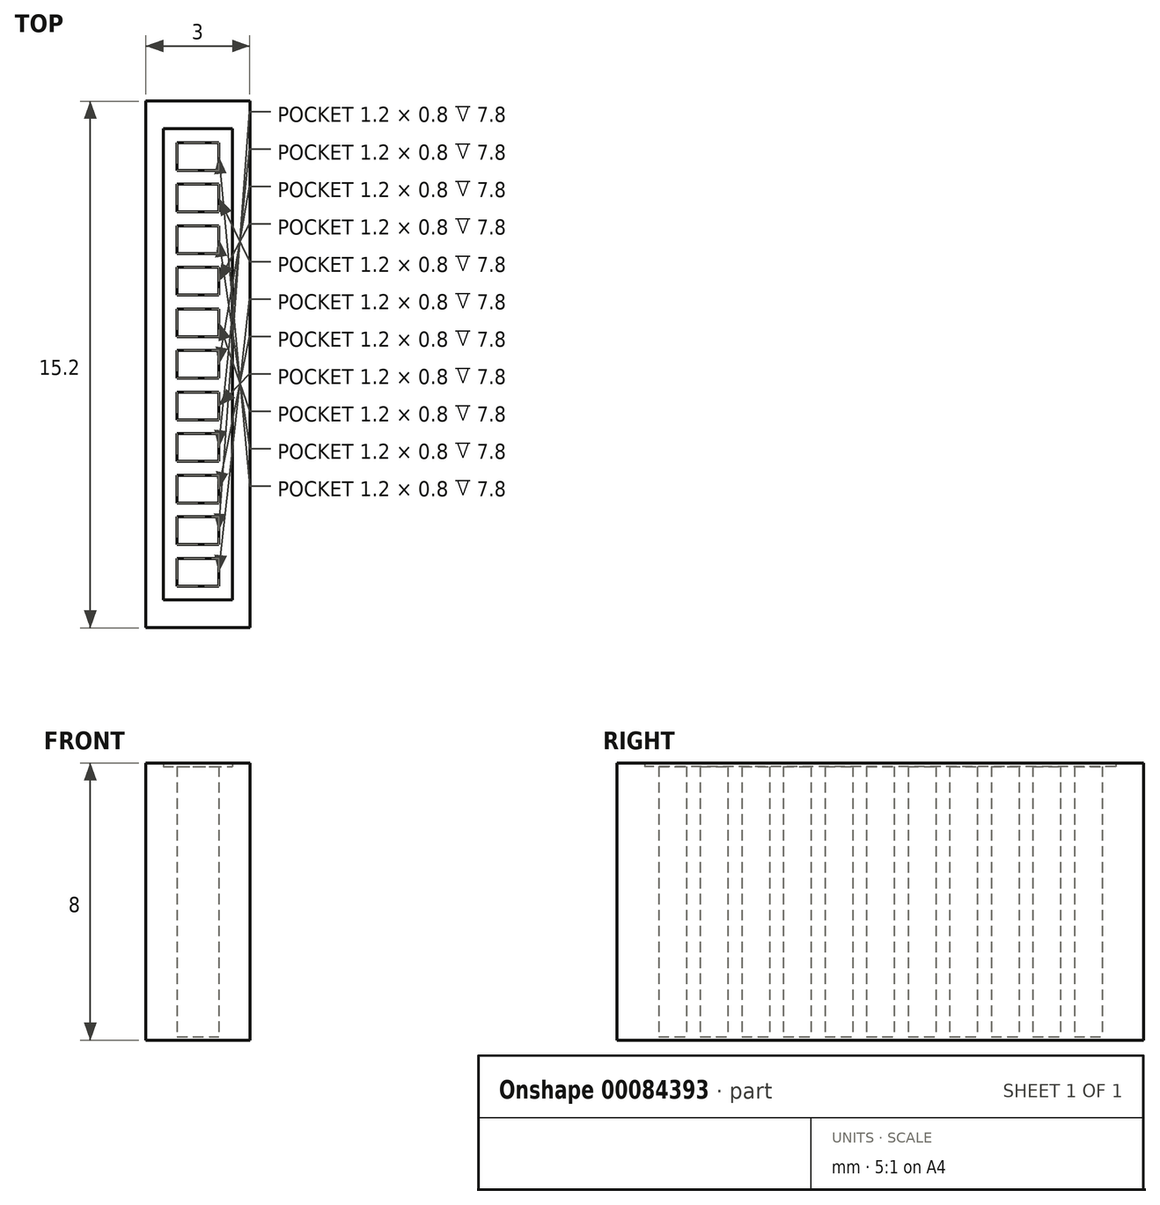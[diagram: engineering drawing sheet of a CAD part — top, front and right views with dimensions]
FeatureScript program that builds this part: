
annotation { "Feature Type Name" : "Feature", "Feature Type Description" : "" }
export const myFeature = defineFeature(function(context is Context, id is Id, definition is map)
    precondition{}
    {
        {
            var Q0;
            Q0=qCreatedBy(makeId("Top.planeOp"),FACE);
            var sketch = newSketch(context, id + "F0", { "sketchPlane" : qUnion([Q0])});
            skLineSegment(sketch, "E0.top", {"start": v(-120.69, 3.96) * mm, "end": v(-117.69, 3.96) * mm});
            skLineSegment(sketch, "E1", {"start": v(-120.19, 4.76) * mm, "end": v(-118.19, 4.76) * mm});
            skLineSegment(sketch, "E2", {"start": v(-120.19, 6.36) * mm, "end": v(-118.19, 6.36) * mm});
            skLineSegment(sketch, "E3", {"start": v(-120.19, 7.16) * mm, "end": v(-118.19, 7.16) * mm});
            skLineSegment(sketch, "E4", {"start": v(-120.19, 8.76) * mm, "end": v(-118.19, 8.76) * mm});
            skLineSegment(sketch, "E5", {"start": v(-120.19, 9.56) * mm, "end": v(-118.19, 9.56) * mm});
            skLineSegment(sketch, "E6", {"start": v(-120.19, 11.16) * mm, "end": v(-118.19, 11.16) * mm});
            skLineSegment(sketch, "E7", {"start": v(-120.19, 11.96) * mm, "end": v(-118.19, 11.96) * mm});
            skLineSegment(sketch, "E8", {"start": v(-120.19, 13.56) * mm, "end": v(-118.19, 13.56) * mm});
            skLineSegment(sketch, "E9", {"start": v(-120.19, 14.36) * mm, "end": v(-118.19, 14.36) * mm});
            skLineSegment(sketch, "E10", {"start": v(-120.19, 15.96) * mm, "end": v(-118.19, 15.96) * mm});
            skLineSegment(sketch, "E11", {"start": v(-120.19, 16.76) * mm, "end": v(-118.19, 16.76) * mm});
            skLineSegment(sketch, "E12", {"start": v(-120.19, 18.36) * mm, "end": v(-118.19, 18.36) * mm});
            skLineSegment(sketch, "E13", {"start": v(-120.19, 19.16) * mm, "end": v(-118.19, 19.16) * mm});
            skLineSegment(sketch, "E14", {"start": v(-120.19, 5.16) * mm, "end": v(-118.19, 5.16) * mm});
            skLineSegment(sketch, "E15", {"start": v(-120.19, 5.96) * mm, "end": v(-118.19, 5.96) * mm});
            skLineSegment(sketch, "E16", {"start": v(-120.19, 7.56) * mm, "end": v(-118.19, 7.56) * mm});
            skLineSegment(sketch, "E17", {"start": v(-120.19, 8.36) * mm, "end": v(-118.19, 8.36) * mm});
            skLineSegment(sketch, "E18", {"start": v(-120.19, 9.96) * mm, "end": v(-118.19, 9.96) * mm});
            skLineSegment(sketch, "E19", {"start": v(-120.19, 10.76) * mm, "end": v(-118.19, 10.76) * mm});
            skLineSegment(sketch, "E20", {"start": v(-120.19, 12.36) * mm, "end": v(-118.19, 12.36) * mm});
            skLineSegment(sketch, "E21", {"start": v(-120.19, 13.16) * mm, "end": v(-118.19, 13.16) * mm});
            skLineSegment(sketch, "E22", {"start": v(-120.19, 14.76) * mm, "end": v(-118.19, 14.76) * mm});
            skLineSegment(sketch, "E23", {"start": v(-120.19, 17.16) * mm, "end": v(-118.19, 17.16) * mm});
            skLineSegment(sketch, "E24", {"start": v(-120.19, 17.96) * mm, "end": v(-118.19, 17.96) * mm});
            skLineSegment(sketch, "E25", {"start": v(-120.19, 15.56) * mm, "end": v(-118.19, 15.56) * mm});
            skLineSegment(sketch, "E26", {"start": v(-117.69, 3.96) * mm, "end": v(-117.69, 19.16) * mm});
            skLineSegment(sketch, "E27", {"start": v(-118.19, 3.96) * mm, "end": v(-118.19, 19.16) * mm});
            skLineSegment(sketch, "E28", {"start": v(-120.69, 3.96) * mm, "end": v(-120.69, 19.16) * mm});
            skLineSegment(sketch, "E29", {"start": v(-120.19, 19.16) * mm, "end": v(-120.19, 3.96) * mm});
            skLineSegment(sketch, "E30", {"start": v(-119.79, 3.96) * mm, "end": v(-119.79, 19.16) * mm});
            skLineSegment(sketch, "E31", {"start": v(-118.59, 3.96) * mm, "end": v(-118.59, 19.16) * mm});
            skLineSegment(sketch, "E32", {"start": v(-120.69, 19.16) * mm, "end": v(-117.69, 19.16) * mm});
            skSolve(sketch);
        }
        {
            var Q0;
            {var subQ0=sQuery(id+"F0.wireOp",EDGE,"E29");var subQ1=sQuery(id+"F0.wireOp",EDGE,"E0.top");var subQ2=makeQuery(id+"F0.imprint","INTERSECT",VERTEX,{"derivedFrom":[subQ1,subQ0]});Q0=makeQuery(id+"F0.imprint","IMPRINT",FACE,{"disambiguationData":[TD([[makeQuery(id+"F0.imprint","IMPRINT",EDGE,{"disambiguationData":[TD([[subQ2,-1.0]])],"derivedFrom":subQ1}),1.0]])]});}
            var Q1;
            {var subQ20=sQuery(id+"F0.wireOp",EDGE,"E28");Q1=makeQuery(id+"F0.imprint","IMPRINT",FACE,{"disambiguationData":[TD([[makeQuery(id+"F0.imprint","IMPRINT",EDGE,{"derivedFrom":subQ20}),-1.0]])]});}
            var Q2;
            {var subQ0=sQuery(id+"F0.wireOp",EDGE,"E30");var subQ1=sQuery(id+"F0.wireOp",EDGE,"E0.top");var subQ2=makeQuery(id+"F0.imprint","INTERSECT",VERTEX,{"derivedFrom":[subQ1,subQ0]});Q2=makeQuery(id+"F0.imprint","IMPRINT",FACE,{"disambiguationData":[TD([[makeQuery(id+"F0.imprint","IMPRINT",EDGE,{"disambiguationData":[TD([[subQ2,-1.0]])],"derivedFrom":subQ1}),1.0]])]});}
            var Q3;
            {var subQ0=sQuery(id+"F0.wireOp",EDGE,"E27");var subQ1=sQuery(id+"F0.wireOp",EDGE,"E0.top");var subQ2=makeQuery(id+"F0.imprint","INTERSECT",VERTEX,{"derivedFrom":[subQ1,subQ0]});Q3=makeQuery(id+"F0.imprint","IMPRINT",FACE,{"disambiguationData":[TD([[makeQuery(id+"F0.imprint","IMPRINT",EDGE,{"disambiguationData":[TD([[subQ2,1.0]])],"derivedFrom":subQ1}),1.0]])]});}
            var Q4;
            {var subQ0=sQuery(id+"F0.wireOp",EDGE,"E29");var subQ1=sQuery(id+"F0.wireOp",EDGE,"E12");var subQ2=makeQuery(id+"F0.imprint","INTERSECT",VERTEX,{"derivedFrom":[subQ1,subQ0]});Q4=makeQuery(id+"F0.imprint","IMPRINT",FACE,{"disambiguationData":[TD([[makeQuery(id+"F0.imprint","IMPRINT",EDGE,{"disambiguationData":[TD([[subQ2,-1.0]])],"derivedFrom":subQ1}),1.0]])]});}
            var Q5;
            {var subQ0=sQuery(id+"F0.wireOp",EDGE,"E30");var subQ1=sQuery(id+"F0.wireOp",EDGE,"E12");var subQ2=makeQuery(id+"F0.imprint","INTERSECT",VERTEX,{"derivedFrom":[subQ1,subQ0]});Q5=makeQuery(id+"F0.imprint","IMPRINT",FACE,{"disambiguationData":[TD([[makeQuery(id+"F0.imprint","IMPRINT",EDGE,{"disambiguationData":[TD([[subQ2,-1.0]])],"derivedFrom":subQ1}),1.0]])]});}
            var Q6;
            {var subQ0=sQuery(id+"F0.wireOp",EDGE,"E27");var subQ1=sQuery(id+"F0.wireOp",EDGE,"E12");var subQ2=makeQuery(id+"F0.imprint","INTERSECT",VERTEX,{"derivedFrom":[subQ1,subQ0]});Q6=makeQuery(id+"F0.imprint","IMPRINT",FACE,{"disambiguationData":[TD([[makeQuery(id+"F0.imprint","IMPRINT",EDGE,{"disambiguationData":[TD([[subQ2,1.0]])],"derivedFrom":subQ1}),1.0]])]});}
            var Q7;
            {var subQ26=sQuery(id+"F0.wireOp",EDGE,"E26");Q7=makeQuery(id+"F0.imprint","IMPRINT",FACE,{"disambiguationData":[TD([[makeQuery(id+"F0.imprint","IMPRINT",EDGE,{"derivedFrom":subQ26}),1.0]])]});}
            extrude(context, id + "F1", {"entities" : qUnion([Q0, Q1, Q2, Q3, Q4, Q5, Q6, Q7]), "depth" : 8 * mm});
        }
        {
            var Q0;
            {var subQ0=sQuery(id+"F0.wireOp",EDGE,"E29");var subQ1=sQuery(id+"F0.wireOp",EDGE,"E1");var subQ2=makeQuery(id+"F0.imprint","INTERSECT",VERTEX,{"derivedFrom":[subQ1,subQ0]});Q0=makeQuery(id+"F0.imprint","IMPRINT",FACE,{"disambiguationData":[TD([[makeQuery(id+"F0.imprint","IMPRINT",EDGE,{"disambiguationData":[TD([[subQ2,-1.0]])],"derivedFrom":subQ1}),1.0]])]});}
            var Q1;
            {var subQ0=sQuery(id+"F0.wireOp",EDGE,"E30");var subQ1=sQuery(id+"F0.wireOp",EDGE,"E1");var subQ2=makeQuery(id+"F0.imprint","INTERSECT",VERTEX,{"derivedFrom":[subQ1,subQ0]});Q1=makeQuery(id+"F0.imprint","IMPRINT",FACE,{"disambiguationData":[TD([[makeQuery(id+"F0.imprint","IMPRINT",EDGE,{"disambiguationData":[TD([[subQ2,-1.0]])],"derivedFrom":subQ1}),1.0]])]});}
            var Q2;
            {var subQ0=sQuery(id+"F0.wireOp",EDGE,"E27");var subQ1=sQuery(id+"F0.wireOp",EDGE,"E1");var subQ2=makeQuery(id+"F0.imprint","INTERSECT",VERTEX,{"derivedFrom":[subQ1,subQ0]});Q2=makeQuery(id+"F0.imprint","IMPRINT",FACE,{"disambiguationData":[TD([[makeQuery(id+"F0.imprint","IMPRINT",EDGE,{"disambiguationData":[TD([[subQ2,1.0]])],"derivedFrom":subQ1}),1.0]])]});}
            var Q3;
            {var subQ0=sQuery(id+"F0.wireOp",EDGE,"E27");var subQ1=sQuery(id+"F0.wireOp",EDGE,"E14");var subQ2=makeQuery(id+"F0.imprint","INTERSECT",VERTEX,{"derivedFrom":[subQ1,subQ0]});Q3=makeQuery(id+"F0.imprint","IMPRINT",FACE,{"disambiguationData":[TD([[makeQuery(id+"F0.imprint","IMPRINT",EDGE,{"disambiguationData":[TD([[subQ2,1.0]])],"derivedFrom":subQ1}),1.0]])]});}
            var Q4;
            {var subQ0=sQuery(id+"F0.wireOp",EDGE,"E27");var subQ1=sQuery(id+"F0.wireOp",EDGE,"E2");var subQ2=makeQuery(id+"F0.imprint","INTERSECT",VERTEX,{"derivedFrom":[subQ1,subQ0]});Q4=makeQuery(id+"F0.imprint","IMPRINT",FACE,{"disambiguationData":[TD([[makeQuery(id+"F0.imprint","IMPRINT",EDGE,{"disambiguationData":[TD([[subQ2,1.0]])],"derivedFrom":subQ1}),-1.0]])]});}
            var Q5;
            {var subQ0=sQuery(id+"F0.wireOp",EDGE,"E30");var subQ1=sQuery(id+"F0.wireOp",EDGE,"E2");var subQ2=makeQuery(id+"F0.imprint","INTERSECT",VERTEX,{"derivedFrom":[subQ1,subQ0]});Q5=makeQuery(id+"F0.imprint","IMPRINT",FACE,{"disambiguationData":[TD([[makeQuery(id+"F0.imprint","IMPRINT",EDGE,{"disambiguationData":[TD([[subQ2,-1.0]])],"derivedFrom":subQ1}),-1.0]])]});}
            var Q6;
            {var subQ0=sQuery(id+"F0.wireOp",EDGE,"E29");var subQ1=sQuery(id+"F0.wireOp",EDGE,"E2");var subQ2=makeQuery(id+"F0.imprint","INTERSECT",VERTEX,{"derivedFrom":[subQ1,subQ0]});Q6=makeQuery(id+"F0.imprint","IMPRINT",FACE,{"disambiguationData":[TD([[makeQuery(id+"F0.imprint","IMPRINT",EDGE,{"disambiguationData":[TD([[subQ2,-1.0]])],"derivedFrom":subQ1}),-1.0]])]});}
            var Q7;
            {var subQ0=sQuery(id+"F0.wireOp",EDGE,"E29");var subQ1=sQuery(id+"F0.wireOp",EDGE,"E14");var subQ2=makeQuery(id+"F0.imprint","INTERSECT",VERTEX,{"derivedFrom":[subQ1,subQ0]});Q7=makeQuery(id+"F0.imprint","IMPRINT",FACE,{"disambiguationData":[TD([[makeQuery(id+"F0.imprint","IMPRINT",EDGE,{"disambiguationData":[TD([[subQ2,-1.0]])],"derivedFrom":subQ1}),1.0]])]});}
            var Q8;
            {var subQ0=sQuery(id+"F0.wireOp",EDGE,"E29");var subQ1=sQuery(id+"F0.wireOp",EDGE,"E2");var subQ2=makeQuery(id+"F0.imprint","INTERSECT",VERTEX,{"derivedFrom":[subQ1,subQ0]});Q8=makeQuery(id+"F0.imprint","IMPRINT",FACE,{"disambiguationData":[TD([[makeQuery(id+"F0.imprint","IMPRINT",EDGE,{"disambiguationData":[TD([[subQ2,-1.0]])],"derivedFrom":subQ1}),1.0]])]});}
            var Q9;
            {var subQ0=sQuery(id+"F0.wireOp",EDGE,"E29");var subQ1=sQuery(id+"F0.wireOp",EDGE,"E4");var subQ2=makeQuery(id+"F0.imprint","INTERSECT",VERTEX,{"derivedFrom":[subQ1,subQ0]});Q9=makeQuery(id+"F0.imprint","IMPRINT",FACE,{"disambiguationData":[TD([[makeQuery(id+"F0.imprint","IMPRINT",EDGE,{"disambiguationData":[TD([[subQ2,-1.0]])],"derivedFrom":subQ1}),-1.0]])]});}
            var Q10;
            {var subQ0=sQuery(id+"F0.wireOp",EDGE,"E29");var subQ1=sQuery(id+"F0.wireOp",EDGE,"E4");var subQ2=makeQuery(id+"F0.imprint","INTERSECT",VERTEX,{"derivedFrom":[subQ1,subQ0]});Q10=makeQuery(id+"F0.imprint","IMPRINT",FACE,{"disambiguationData":[TD([[makeQuery(id+"F0.imprint","IMPRINT",EDGE,{"disambiguationData":[TD([[subQ2,-1.0]])],"derivedFrom":subQ1}),1.0]])]});}
            var Q11;
            {var subQ0=sQuery(id+"F0.wireOp",EDGE,"E29");var subQ1=sQuery(id+"F0.wireOp",EDGE,"E5");var subQ2=makeQuery(id+"F0.imprint","INTERSECT",VERTEX,{"derivedFrom":[subQ1,subQ0]});Q11=makeQuery(id+"F0.imprint","IMPRINT",FACE,{"disambiguationData":[TD([[makeQuery(id+"F0.imprint","IMPRINT",EDGE,{"disambiguationData":[TD([[subQ2,-1.0]])],"derivedFrom":subQ1}),1.0]])]});}
            var Q12;
            {var subQ0=sQuery(id+"F0.wireOp",EDGE,"E29");var subQ1=sQuery(id+"F0.wireOp",EDGE,"E18");var subQ2=makeQuery(id+"F0.imprint","INTERSECT",VERTEX,{"derivedFrom":[subQ1,subQ0]});Q12=makeQuery(id+"F0.imprint","IMPRINT",FACE,{"disambiguationData":[TD([[makeQuery(id+"F0.imprint","IMPRINT",EDGE,{"disambiguationData":[TD([[subQ2,-1.0]])],"derivedFrom":subQ1}),1.0]])]});}
            var Q13;
            {var subQ0=sQuery(id+"F0.wireOp",EDGE,"E29");var subQ1=sQuery(id+"F0.wireOp",EDGE,"E6");var subQ2=makeQuery(id+"F0.imprint","INTERSECT",VERTEX,{"derivedFrom":[subQ1,subQ0]});Q13=makeQuery(id+"F0.imprint","IMPRINT",FACE,{"disambiguationData":[TD([[makeQuery(id+"F0.imprint","IMPRINT",EDGE,{"disambiguationData":[TD([[subQ2,-1.0]])],"derivedFrom":subQ1}),1.0]])]});}
            var Q14;
            {var subQ0=sQuery(id+"F0.wireOp",EDGE,"E29");var subQ1=sQuery(id+"F0.wireOp",EDGE,"E20");var subQ2=makeQuery(id+"F0.imprint","INTERSECT",VERTEX,{"derivedFrom":[subQ1,subQ0]});Q14=makeQuery(id+"F0.imprint","IMPRINT",FACE,{"disambiguationData":[TD([[makeQuery(id+"F0.imprint","IMPRINT",EDGE,{"disambiguationData":[TD([[subQ2,-1.0]])],"derivedFrom":subQ1}),1.0]])]});}
            var Q15;
            {var subQ0=sQuery(id+"F0.wireOp",EDGE,"E29");var subQ1=sQuery(id+"F0.wireOp",EDGE,"E8");var subQ2=makeQuery(id+"F0.imprint","INTERSECT",VERTEX,{"derivedFrom":[subQ1,subQ0]});Q15=makeQuery(id+"F0.imprint","IMPRINT",FACE,{"disambiguationData":[TD([[makeQuery(id+"F0.imprint","IMPRINT",EDGE,{"disambiguationData":[TD([[subQ2,-1.0]])],"derivedFrom":subQ1}),-1.0]])]});}
            var Q16;
            {var subQ0=sQuery(id+"F0.wireOp",EDGE,"E29");var subQ1=sQuery(id+"F0.wireOp",EDGE,"E9");var subQ2=makeQuery(id+"F0.imprint","INTERSECT",VERTEX,{"derivedFrom":[subQ1,subQ0]});Q16=makeQuery(id+"F0.imprint","IMPRINT",FACE,{"disambiguationData":[TD([[makeQuery(id+"F0.imprint","IMPRINT",EDGE,{"disambiguationData":[TD([[subQ2,-1.0]])],"derivedFrom":subQ1}),1.0]])]});}
            var Q17;
            {var subQ0=sQuery(id+"F0.wireOp",EDGE,"E29");var subQ1=sQuery(id+"F0.wireOp",EDGE,"E22");var subQ2=makeQuery(id+"F0.imprint","INTERSECT",VERTEX,{"derivedFrom":[subQ1,subQ0]});Q17=makeQuery(id+"F0.imprint","IMPRINT",FACE,{"disambiguationData":[TD([[makeQuery(id+"F0.imprint","IMPRINT",EDGE,{"disambiguationData":[TD([[subQ2,-1.0]])],"derivedFrom":subQ1}),1.0]])]});}
            var Q18;
            {var subQ0=sQuery(id+"F0.wireOp",EDGE,"E29");var subQ1=sQuery(id+"F0.wireOp",EDGE,"E10");var subQ2=makeQuery(id+"F0.imprint","INTERSECT",VERTEX,{"derivedFrom":[subQ1,subQ0]});Q18=makeQuery(id+"F0.imprint","IMPRINT",FACE,{"disambiguationData":[TD([[makeQuery(id+"F0.imprint","IMPRINT",EDGE,{"disambiguationData":[TD([[subQ2,-1.0]])],"derivedFrom":subQ1}),-1.0]])]});}
            var Q19;
            {var subQ0=sQuery(id+"F0.wireOp",EDGE,"E29");var subQ1=sQuery(id+"F0.wireOp",EDGE,"E10");var subQ2=makeQuery(id+"F0.imprint","INTERSECT",VERTEX,{"derivedFrom":[subQ1,subQ0]});Q19=makeQuery(id+"F0.imprint","IMPRINT",FACE,{"disambiguationData":[TD([[makeQuery(id+"F0.imprint","IMPRINT",EDGE,{"disambiguationData":[TD([[subQ2,-1.0]])],"derivedFrom":subQ1}),1.0]])]});}
            var Q20;
            {var subQ0=sQuery(id+"F0.wireOp",EDGE,"E29");var subQ1=sQuery(id+"F0.wireOp",EDGE,"E11");var subQ2=makeQuery(id+"F0.imprint","INTERSECT",VERTEX,{"derivedFrom":[subQ1,subQ0]});Q20=makeQuery(id+"F0.imprint","IMPRINT",FACE,{"disambiguationData":[TD([[makeQuery(id+"F0.imprint","IMPRINT",EDGE,{"disambiguationData":[TD([[subQ2,-1.0]])],"derivedFrom":subQ1}),1.0]])]});}
            var Q21;
            {var subQ0=sQuery(id+"F0.wireOp",EDGE,"E29");var subQ1=sQuery(id+"F0.wireOp",EDGE,"E23");var subQ2=makeQuery(id+"F0.imprint","INTERSECT",VERTEX,{"derivedFrom":[subQ1,subQ0]});Q21=makeQuery(id+"F0.imprint","IMPRINT",FACE,{"disambiguationData":[TD([[makeQuery(id+"F0.imprint","IMPRINT",EDGE,{"disambiguationData":[TD([[subQ2,-1.0]])],"derivedFrom":subQ1}),1.0]])]});}
            var Q22;
            {var subQ0=sQuery(id+"F0.wireOp",EDGE,"E29");var subQ1=sQuery(id+"F0.wireOp",EDGE,"E12");var subQ2=makeQuery(id+"F0.imprint","INTERSECT",VERTEX,{"derivedFrom":[subQ1,subQ0]});Q22=makeQuery(id+"F0.imprint","IMPRINT",FACE,{"disambiguationData":[TD([[makeQuery(id+"F0.imprint","IMPRINT",EDGE,{"disambiguationData":[TD([[subQ2,-1.0]])],"derivedFrom":subQ1}),-1.0]])]});}
            var Q23;
            {var subQ0=sQuery(id+"F0.wireOp",EDGE,"E30");var subQ1=sQuery(id+"F0.wireOp",EDGE,"E12");var subQ2=makeQuery(id+"F0.imprint","INTERSECT",VERTEX,{"derivedFrom":[subQ1,subQ0]});Q23=makeQuery(id+"F0.imprint","IMPRINT",FACE,{"disambiguationData":[TD([[makeQuery(id+"F0.imprint","IMPRINT",EDGE,{"disambiguationData":[TD([[subQ2,-1.0]])],"derivedFrom":subQ1}),-1.0]])]});}
            var Q24;
            {var subQ0=sQuery(id+"F0.wireOp",EDGE,"E27");var subQ1=sQuery(id+"F0.wireOp",EDGE,"E12");var subQ2=makeQuery(id+"F0.imprint","INTERSECT",VERTEX,{"derivedFrom":[subQ1,subQ0]});Q24=makeQuery(id+"F0.imprint","IMPRINT",FACE,{"disambiguationData":[TD([[makeQuery(id+"F0.imprint","IMPRINT",EDGE,{"disambiguationData":[TD([[subQ2,1.0]])],"derivedFrom":subQ1}),-1.0]])]});}
            var Q25;
            {var subQ0=sQuery(id+"F0.wireOp",EDGE,"E27");var subQ1=sQuery(id+"F0.wireOp",EDGE,"E23");var subQ2=makeQuery(id+"F0.imprint","INTERSECT",VERTEX,{"derivedFrom":[subQ1,subQ0]});Q25=makeQuery(id+"F0.imprint","IMPRINT",FACE,{"disambiguationData":[TD([[makeQuery(id+"F0.imprint","IMPRINT",EDGE,{"disambiguationData":[TD([[subQ2,1.0]])],"derivedFrom":subQ1}),1.0]])]});}
            var Q26;
            {var subQ0=sQuery(id+"F0.wireOp",EDGE,"E27");var subQ1=sQuery(id+"F0.wireOp",EDGE,"E11");var subQ2=makeQuery(id+"F0.imprint","INTERSECT",VERTEX,{"derivedFrom":[subQ1,subQ0]});Q26=makeQuery(id+"F0.imprint","IMPRINT",FACE,{"disambiguationData":[TD([[makeQuery(id+"F0.imprint","IMPRINT",EDGE,{"disambiguationData":[TD([[subQ2,1.0]])],"derivedFrom":subQ1}),1.0]])]});}
            var Q27;
            {var subQ0=sQuery(id+"F0.wireOp",EDGE,"E27");var subQ1=sQuery(id+"F0.wireOp",EDGE,"E10");var subQ2=makeQuery(id+"F0.imprint","INTERSECT",VERTEX,{"derivedFrom":[subQ1,subQ0]});Q27=makeQuery(id+"F0.imprint","IMPRINT",FACE,{"disambiguationData":[TD([[makeQuery(id+"F0.imprint","IMPRINT",EDGE,{"disambiguationData":[TD([[subQ2,1.0]])],"derivedFrom":subQ1}),1.0]])]});}
            var Q28;
            {var subQ0=sQuery(id+"F0.wireOp",EDGE,"E27");var subQ1=sQuery(id+"F0.wireOp",EDGE,"E10");var subQ2=makeQuery(id+"F0.imprint","INTERSECT",VERTEX,{"derivedFrom":[subQ1,subQ0]});Q28=makeQuery(id+"F0.imprint","IMPRINT",FACE,{"disambiguationData":[TD([[makeQuery(id+"F0.imprint","IMPRINT",EDGE,{"disambiguationData":[TD([[subQ2,1.0]])],"derivedFrom":subQ1}),-1.0]])]});}
            var Q29;
            {var subQ0=sQuery(id+"F0.wireOp",EDGE,"E27");var subQ1=sQuery(id+"F0.wireOp",EDGE,"E22");var subQ2=makeQuery(id+"F0.imprint","INTERSECT",VERTEX,{"derivedFrom":[subQ1,subQ0]});Q29=makeQuery(id+"F0.imprint","IMPRINT",FACE,{"disambiguationData":[TD([[makeQuery(id+"F0.imprint","IMPRINT",EDGE,{"disambiguationData":[TD([[subQ2,1.0]])],"derivedFrom":subQ1}),1.0]])]});}
            var Q30;
            {var subQ0=sQuery(id+"F0.wireOp",EDGE,"E27");var subQ1=sQuery(id+"F0.wireOp",EDGE,"E8");var subQ2=makeQuery(id+"F0.imprint","INTERSECT",VERTEX,{"derivedFrom":[subQ1,subQ0]});Q30=makeQuery(id+"F0.imprint","IMPRINT",FACE,{"disambiguationData":[TD([[makeQuery(id+"F0.imprint","IMPRINT",EDGE,{"disambiguationData":[TD([[subQ2,1.0]])],"derivedFrom":subQ1}),1.0]])]});}
            var Q31;
            {var subQ0=sQuery(id+"F0.wireOp",EDGE,"E27");var subQ1=sQuery(id+"F0.wireOp",EDGE,"E9");var subQ2=makeQuery(id+"F0.imprint","INTERSECT",VERTEX,{"derivedFrom":[subQ1,subQ0]});Q31=makeQuery(id+"F0.imprint","IMPRINT",FACE,{"disambiguationData":[TD([[makeQuery(id+"F0.imprint","IMPRINT",EDGE,{"disambiguationData":[TD([[subQ2,1.0]])],"derivedFrom":subQ1}),1.0]])]});}
            var Q32;
            {var subQ0=sQuery(id+"F0.wireOp",EDGE,"E27");var subQ1=sQuery(id+"F0.wireOp",EDGE,"E6");var subQ2=makeQuery(id+"F0.imprint","INTERSECT",VERTEX,{"derivedFrom":[subQ1,subQ0]});Q32=makeQuery(id+"F0.imprint","IMPRINT",FACE,{"disambiguationData":[TD([[makeQuery(id+"F0.imprint","IMPRINT",EDGE,{"disambiguationData":[TD([[subQ2,1.0]])],"derivedFrom":subQ1}),1.0]])]});}
            var Q33;
            {var subQ0=sQuery(id+"F0.wireOp",EDGE,"E27");var subQ1=sQuery(id+"F0.wireOp",EDGE,"E6");var subQ2=makeQuery(id+"F0.imprint","INTERSECT",VERTEX,{"derivedFrom":[subQ1,subQ0]});Q33=makeQuery(id+"F0.imprint","IMPRINT",FACE,{"disambiguationData":[TD([[makeQuery(id+"F0.imprint","IMPRINT",EDGE,{"disambiguationData":[TD([[subQ2,1.0]])],"derivedFrom":subQ1}),-1.0]])]});}
            var Q34;
            {var subQ0=sQuery(id+"F0.wireOp",EDGE,"E27");var subQ1=sQuery(id+"F0.wireOp",EDGE,"E18");var subQ2=makeQuery(id+"F0.imprint","INTERSECT",VERTEX,{"derivedFrom":[subQ1,subQ0]});Q34=makeQuery(id+"F0.imprint","IMPRINT",FACE,{"disambiguationData":[TD([[makeQuery(id+"F0.imprint","IMPRINT",EDGE,{"disambiguationData":[TD([[subQ2,1.0]])],"derivedFrom":subQ1}),1.0]])]});}
            var Q35;
            {var subQ0=sQuery(id+"F0.wireOp",EDGE,"E27");var subQ1=sQuery(id+"F0.wireOp",EDGE,"E4");var subQ2=makeQuery(id+"F0.imprint","INTERSECT",VERTEX,{"derivedFrom":[subQ1,subQ0]});Q35=makeQuery(id+"F0.imprint","IMPRINT",FACE,{"disambiguationData":[TD([[makeQuery(id+"F0.imprint","IMPRINT",EDGE,{"disambiguationData":[TD([[subQ2,1.0]])],"derivedFrom":subQ1}),-1.0]])]});}
            var Q36;
            {var subQ0=sQuery(id+"F0.wireOp",EDGE,"E27");var subQ1=sQuery(id+"F0.wireOp",EDGE,"E16");var subQ2=makeQuery(id+"F0.imprint","INTERSECT",VERTEX,{"derivedFrom":[subQ1,subQ0]});Q36=makeQuery(id+"F0.imprint","IMPRINT",FACE,{"disambiguationData":[TD([[makeQuery(id+"F0.imprint","IMPRINT",EDGE,{"disambiguationData":[TD([[subQ2,1.0]])],"derivedFrom":subQ1}),1.0]])]});}
            var Q37;
            {var subQ0=sQuery(id+"F0.wireOp",EDGE,"E27");var subQ1=sQuery(id+"F0.wireOp",EDGE,"E3");var subQ2=makeQuery(id+"F0.imprint","INTERSECT",VERTEX,{"derivedFrom":[subQ1,subQ0]});Q37=makeQuery(id+"F0.imprint","IMPRINT",FACE,{"disambiguationData":[TD([[makeQuery(id+"F0.imprint","IMPRINT",EDGE,{"disambiguationData":[TD([[subQ2,1.0]])],"derivedFrom":subQ1}),1.0]])]});}
            var Q38;
            {var subQ0=sQuery(id+"F0.wireOp",EDGE,"E27");var subQ1=sQuery(id+"F0.wireOp",EDGE,"E2");var subQ2=makeQuery(id+"F0.imprint","INTERSECT",VERTEX,{"derivedFrom":[subQ1,subQ0]});Q38=makeQuery(id+"F0.imprint","IMPRINT",FACE,{"disambiguationData":[TD([[makeQuery(id+"F0.imprint","IMPRINT",EDGE,{"disambiguationData":[TD([[subQ2,1.0]])],"derivedFrom":subQ1}),1.0]])]});}
            var Q39;
            {var subQ0=sQuery(id+"F0.wireOp",EDGE,"E29");var subQ1=sQuery(id+"F0.wireOp",EDGE,"E3");var subQ2=makeQuery(id+"F0.imprint","INTERSECT",VERTEX,{"derivedFrom":[subQ1,subQ0]});Q39=makeQuery(id+"F0.imprint","IMPRINT",FACE,{"disambiguationData":[TD([[makeQuery(id+"F0.imprint","IMPRINT",EDGE,{"disambiguationData":[TD([[subQ2,-1.0]])],"derivedFrom":subQ1}),1.0]])]});}
            var Q40;
            {var subQ0=sQuery(id+"F0.wireOp",EDGE,"E29");var subQ1=sQuery(id+"F0.wireOp",EDGE,"E6");var subQ2=makeQuery(id+"F0.imprint","INTERSECT",VERTEX,{"derivedFrom":[subQ1,subQ0]});Q40=makeQuery(id+"F0.imprint","IMPRINT",FACE,{"disambiguationData":[TD([[makeQuery(id+"F0.imprint","IMPRINT",EDGE,{"disambiguationData":[TD([[subQ2,-1.0]])],"derivedFrom":subQ1}),-1.0]])]});}
            var Q41;
            {var subQ0=sQuery(id+"F0.wireOp",EDGE,"E29");var subQ1=sQuery(id+"F0.wireOp",EDGE,"E20");var subQ2=makeQuery(id+"F0.imprint","INTERSECT",VERTEX,{"derivedFrom":[subQ1,subQ0]});Q41=makeQuery(id+"F0.imprint","IMPRINT",FACE,{"disambiguationData":[TD([[makeQuery(id+"F0.imprint","IMPRINT",EDGE,{"disambiguationData":[TD([[subQ2,-1.0]])],"derivedFrom":subQ1}),-1.0]])]});}
            var Q42;
            {var subQ0=sQuery(id+"F0.wireOp",EDGE,"E29");var subQ1=sQuery(id+"F0.wireOp",EDGE,"E8");var subQ2=makeQuery(id+"F0.imprint","INTERSECT",VERTEX,{"derivedFrom":[subQ1,subQ0]});Q42=makeQuery(id+"F0.imprint","IMPRINT",FACE,{"disambiguationData":[TD([[makeQuery(id+"F0.imprint","IMPRINT",EDGE,{"disambiguationData":[TD([[subQ2,-1.0]])],"derivedFrom":subQ1}),1.0]])]});}
            var Q43;
            {var subQ0=sQuery(id+"F0.wireOp",EDGE,"E29");var subQ1=sQuery(id+"F0.wireOp",EDGE,"E16");var subQ2=makeQuery(id+"F0.imprint","INTERSECT",VERTEX,{"derivedFrom":[subQ1,subQ0]});Q43=makeQuery(id+"F0.imprint","IMPRINT",FACE,{"disambiguationData":[TD([[makeQuery(id+"F0.imprint","IMPRINT",EDGE,{"disambiguationData":[TD([[subQ2,-1.0]])],"derivedFrom":subQ1}),1.0]])]});}
            var Q44;
            {var subQ0=sQuery(id+"F0.wireOp",EDGE,"E30");var subQ1=sQuery(id+"F0.wireOp",EDGE,"E11");var subQ2=makeQuery(id+"F0.imprint","INTERSECT",VERTEX,{"derivedFrom":[subQ1,subQ0]});Q44=makeQuery(id+"F0.imprint","IMPRINT",FACE,{"disambiguationData":[TD([[makeQuery(id+"F0.imprint","IMPRINT",EDGE,{"disambiguationData":[TD([[subQ2,-1.0]])],"derivedFrom":subQ1}),1.0]])]});}
            var Q45;
            {var subQ0=sQuery(id+"F0.wireOp",EDGE,"E30");var subQ1=sQuery(id+"F0.wireOp",EDGE,"E10");var subQ2=makeQuery(id+"F0.imprint","INTERSECT",VERTEX,{"derivedFrom":[subQ1,subQ0]});Q45=makeQuery(id+"F0.imprint","IMPRINT",FACE,{"disambiguationData":[TD([[makeQuery(id+"F0.imprint","IMPRINT",EDGE,{"disambiguationData":[TD([[subQ2,-1.0]])],"derivedFrom":subQ1}),-1.0]])]});}
            var Q46;
            {var subQ0=sQuery(id+"F0.wireOp",EDGE,"E30");var subQ1=sQuery(id+"F0.wireOp",EDGE,"E9");var subQ2=makeQuery(id+"F0.imprint","INTERSECT",VERTEX,{"derivedFrom":[subQ1,subQ0]});Q46=makeQuery(id+"F0.imprint","IMPRINT",FACE,{"disambiguationData":[TD([[makeQuery(id+"F0.imprint","IMPRINT",EDGE,{"disambiguationData":[TD([[subQ2,-1.0]])],"derivedFrom":subQ1}),1.0]])]});}
            var Q47;
            {var subQ0=sQuery(id+"F0.wireOp",EDGE,"E30");var subQ1=sQuery(id+"F0.wireOp",EDGE,"E8");var subQ2=makeQuery(id+"F0.imprint","INTERSECT",VERTEX,{"derivedFrom":[subQ1,subQ0]});Q47=makeQuery(id+"F0.imprint","IMPRINT",FACE,{"disambiguationData":[TD([[makeQuery(id+"F0.imprint","IMPRINT",EDGE,{"disambiguationData":[TD([[subQ2,-1.0]])],"derivedFrom":subQ1}),-1.0]])]});}
            var Q48;
            {var subQ0=sQuery(id+"F0.wireOp",EDGE,"E30");var subQ1=sQuery(id+"F0.wireOp",EDGE,"E20");var subQ2=makeQuery(id+"F0.imprint","INTERSECT",VERTEX,{"derivedFrom":[subQ1,subQ0]});Q48=makeQuery(id+"F0.imprint","IMPRINT",FACE,{"disambiguationData":[TD([[makeQuery(id+"F0.imprint","IMPRINT",EDGE,{"disambiguationData":[TD([[subQ2,-1.0]])],"derivedFrom":subQ1}),-1.0]])]});}
            var Q49;
            {var subQ0=sQuery(id+"F0.wireOp",EDGE,"E30");var subQ1=sQuery(id+"F0.wireOp",EDGE,"E6");var subQ2=makeQuery(id+"F0.imprint","INTERSECT",VERTEX,{"derivedFrom":[subQ1,subQ0]});Q49=makeQuery(id+"F0.imprint","IMPRINT",FACE,{"disambiguationData":[TD([[makeQuery(id+"F0.imprint","IMPRINT",EDGE,{"disambiguationData":[TD([[subQ2,-1.0]])],"derivedFrom":subQ1}),-1.0]])]});}
            var Q50;
            {var subQ0=sQuery(id+"F0.wireOp",EDGE,"E30");var subQ1=sQuery(id+"F0.wireOp",EDGE,"E5");var subQ2=makeQuery(id+"F0.imprint","INTERSECT",VERTEX,{"derivedFrom":[subQ1,subQ0]});Q50=makeQuery(id+"F0.imprint","IMPRINT",FACE,{"disambiguationData":[TD([[makeQuery(id+"F0.imprint","IMPRINT",EDGE,{"disambiguationData":[TD([[subQ2,-1.0]])],"derivedFrom":subQ1}),1.0]])]});}
            var Q51;
            {var subQ0=sQuery(id+"F0.wireOp",EDGE,"E30");var subQ1=sQuery(id+"F0.wireOp",EDGE,"E4");var subQ2=makeQuery(id+"F0.imprint","INTERSECT",VERTEX,{"derivedFrom":[subQ1,subQ0]});Q51=makeQuery(id+"F0.imprint","IMPRINT",FACE,{"disambiguationData":[TD([[makeQuery(id+"F0.imprint","IMPRINT",EDGE,{"disambiguationData":[TD([[subQ2,-1.0]])],"derivedFrom":subQ1}),-1.0]])]});}
            var Q52;
            {var subQ0=sQuery(id+"F0.wireOp",EDGE,"E30");var subQ1=sQuery(id+"F0.wireOp",EDGE,"E3");var subQ2=makeQuery(id+"F0.imprint","INTERSECT",VERTEX,{"derivedFrom":[subQ1,subQ0]});Q52=makeQuery(id+"F0.imprint","IMPRINT",FACE,{"disambiguationData":[TD([[makeQuery(id+"F0.imprint","IMPRINT",EDGE,{"disambiguationData":[TD([[subQ2,-1.0]])],"derivedFrom":subQ1}),1.0]])]});}
            var Q53;
            {var subQ0=sQuery(id+"F0.wireOp",EDGE,"E27");var subQ1=sQuery(id+"F0.wireOp",EDGE,"E4");var subQ2=makeQuery(id+"F0.imprint","INTERSECT",VERTEX,{"derivedFrom":[subQ1,subQ0]});Q53=makeQuery(id+"F0.imprint","IMPRINT",FACE,{"disambiguationData":[TD([[makeQuery(id+"F0.imprint","IMPRINT",EDGE,{"disambiguationData":[TD([[subQ2,1.0]])],"derivedFrom":subQ1}),1.0]])]});}
            var Q54;
            {var subQ0=sQuery(id+"F0.wireOp",EDGE,"E27");var subQ1=sQuery(id+"F0.wireOp",EDGE,"E5");var subQ2=makeQuery(id+"F0.imprint","INTERSECT",VERTEX,{"derivedFrom":[subQ1,subQ0]});Q54=makeQuery(id+"F0.imprint","IMPRINT",FACE,{"disambiguationData":[TD([[makeQuery(id+"F0.imprint","IMPRINT",EDGE,{"disambiguationData":[TD([[subQ2,1.0]])],"derivedFrom":subQ1}),1.0]])]});}
            var Q55;
            {var subQ0=sQuery(id+"F0.wireOp",EDGE,"E27");var subQ1=sQuery(id+"F0.wireOp",EDGE,"E20");var subQ2=makeQuery(id+"F0.imprint","INTERSECT",VERTEX,{"derivedFrom":[subQ1,subQ0]});Q55=makeQuery(id+"F0.imprint","IMPRINT",FACE,{"disambiguationData":[TD([[makeQuery(id+"F0.imprint","IMPRINT",EDGE,{"disambiguationData":[TD([[subQ2,1.0]])],"derivedFrom":subQ1}),-1.0]])]});}
            var Q56;
            {var subQ0=sQuery(id+"F0.wireOp",EDGE,"E27");var subQ1=sQuery(id+"F0.wireOp",EDGE,"E20");var subQ2=makeQuery(id+"F0.imprint","INTERSECT",VERTEX,{"derivedFrom":[subQ1,subQ0]});Q56=makeQuery(id+"F0.imprint","IMPRINT",FACE,{"disambiguationData":[TD([[makeQuery(id+"F0.imprint","IMPRINT",EDGE,{"disambiguationData":[TD([[subQ2,1.0]])],"derivedFrom":subQ1}),1.0]])]});}
            var Q57;
            {var subQ0=sQuery(id+"F0.wireOp",EDGE,"E27");var subQ1=sQuery(id+"F0.wireOp",EDGE,"E8");var subQ2=makeQuery(id+"F0.imprint","INTERSECT",VERTEX,{"derivedFrom":[subQ1,subQ0]});Q57=makeQuery(id+"F0.imprint","IMPRINT",FACE,{"disambiguationData":[TD([[makeQuery(id+"F0.imprint","IMPRINT",EDGE,{"disambiguationData":[TD([[subQ2,1.0]])],"derivedFrom":subQ1}),-1.0]])]});}
            extrude(context, id + "F2", {"entities" : qUnion([Q0, Q1, Q2, Q3, Q4, Q5, Q6, Q7, Q8, Q9, Q10, Q11, Q12, Q13, Q14, Q15, Q16, Q17, Q18, Q19, Q20, Q21, Q22, Q23, Q24, Q25, Q26, Q27, Q28, Q29, Q30, Q31, Q32, Q33, Q34, Q35, Q36, Q37, Q38, Q39, Q40, Q41, Q42, Q43, Q44, Q45, Q46, Q47, Q48, Q49, Q50, Q51, Q52, Q53, Q54, Q55, Q56, Q57]), "operationType" : NewBodyOperationType.ADD, "depth" : 7.9 * mm});
        }
        {
            var Q0;
            {var subQ0=sQuery(id+"F0.wireOp",EDGE,"E30");var subQ1=sQuery(id+"F0.wireOp",EDGE,"E23");var subQ2=makeQuery(id+"F0.imprint","INTERSECT",VERTEX,{"derivedFrom":[subQ1,subQ0]});Q0=makeQuery(id+"F0.imprint","IMPRINT",FACE,{"disambiguationData":[TD([[makeQuery(id+"F0.imprint","IMPRINT",EDGE,{"disambiguationData":[TD([[subQ2,-1.0]])],"derivedFrom":subQ1}),1.0]])]});}
            var Q1;
            {var subQ0=sQuery(id+"F0.wireOp",EDGE,"E30");var subQ1=sQuery(id+"F0.wireOp",EDGE,"E10");var subQ2=makeQuery(id+"F0.imprint","INTERSECT",VERTEX,{"derivedFrom":[subQ1,subQ0]});Q1=makeQuery(id+"F0.imprint","IMPRINT",FACE,{"disambiguationData":[TD([[makeQuery(id+"F0.imprint","IMPRINT",EDGE,{"disambiguationData":[TD([[subQ2,-1.0]])],"derivedFrom":subQ1}),1.0]])]});}
            var Q2;
            {var subQ0=sQuery(id+"F0.wireOp",EDGE,"E30");var subQ1=sQuery(id+"F0.wireOp",EDGE,"E22");var subQ2=makeQuery(id+"F0.imprint","INTERSECT",VERTEX,{"derivedFrom":[subQ1,subQ0]});Q2=makeQuery(id+"F0.imprint","IMPRINT",FACE,{"disambiguationData":[TD([[makeQuery(id+"F0.imprint","IMPRINT",EDGE,{"disambiguationData":[TD([[subQ2,-1.0]])],"derivedFrom":subQ1}),1.0]])]});}
            var Q3;
            {var subQ0=sQuery(id+"F0.wireOp",EDGE,"E30");var subQ1=sQuery(id+"F0.wireOp",EDGE,"E8");var subQ2=makeQuery(id+"F0.imprint","INTERSECT",VERTEX,{"derivedFrom":[subQ1,subQ0]});Q3=makeQuery(id+"F0.imprint","IMPRINT",FACE,{"disambiguationData":[TD([[makeQuery(id+"F0.imprint","IMPRINT",EDGE,{"disambiguationData":[TD([[subQ2,-1.0]])],"derivedFrom":subQ1}),1.0]])]});}
            var Q4;
            {var subQ0=sQuery(id+"F0.wireOp",EDGE,"E30");var subQ1=sQuery(id+"F0.wireOp",EDGE,"E20");var subQ2=makeQuery(id+"F0.imprint","INTERSECT",VERTEX,{"derivedFrom":[subQ1,subQ0]});Q4=makeQuery(id+"F0.imprint","IMPRINT",FACE,{"disambiguationData":[TD([[makeQuery(id+"F0.imprint","IMPRINT",EDGE,{"disambiguationData":[TD([[subQ2,-1.0]])],"derivedFrom":subQ1}),1.0]])]});}
            var Q5;
            {var subQ0=sQuery(id+"F0.wireOp",EDGE,"E30");var subQ1=sQuery(id+"F0.wireOp",EDGE,"E6");var subQ2=makeQuery(id+"F0.imprint","INTERSECT",VERTEX,{"derivedFrom":[subQ1,subQ0]});Q5=makeQuery(id+"F0.imprint","IMPRINT",FACE,{"disambiguationData":[TD([[makeQuery(id+"F0.imprint","IMPRINT",EDGE,{"disambiguationData":[TD([[subQ2,-1.0]])],"derivedFrom":subQ1}),1.0]])]});}
            var Q6;
            {var subQ0=sQuery(id+"F0.wireOp",EDGE,"E30");var subQ1=sQuery(id+"F0.wireOp",EDGE,"E18");var subQ2=makeQuery(id+"F0.imprint","INTERSECT",VERTEX,{"derivedFrom":[subQ1,subQ0]});Q6=makeQuery(id+"F0.imprint","IMPRINT",FACE,{"disambiguationData":[TD([[makeQuery(id+"F0.imprint","IMPRINT",EDGE,{"disambiguationData":[TD([[subQ2,-1.0]])],"derivedFrom":subQ1}),1.0]])]});}
            var Q7;
            {var subQ0=sQuery(id+"F0.wireOp",EDGE,"E30");var subQ1=sQuery(id+"F0.wireOp",EDGE,"E4");var subQ2=makeQuery(id+"F0.imprint","INTERSECT",VERTEX,{"derivedFrom":[subQ1,subQ0]});Q7=makeQuery(id+"F0.imprint","IMPRINT",FACE,{"disambiguationData":[TD([[makeQuery(id+"F0.imprint","IMPRINT",EDGE,{"disambiguationData":[TD([[subQ2,-1.0]])],"derivedFrom":subQ1}),1.0]])]});}
            var Q8;
            {var subQ0=sQuery(id+"F0.wireOp",EDGE,"E30");var subQ1=sQuery(id+"F0.wireOp",EDGE,"E16");var subQ2=makeQuery(id+"F0.imprint","INTERSECT",VERTEX,{"derivedFrom":[subQ1,subQ0]});Q8=makeQuery(id+"F0.imprint","IMPRINT",FACE,{"disambiguationData":[TD([[makeQuery(id+"F0.imprint","IMPRINT",EDGE,{"disambiguationData":[TD([[subQ2,-1.0]])],"derivedFrom":subQ1}),1.0]])]});}
            var Q9;
            {var subQ0=sQuery(id+"F0.wireOp",EDGE,"E30");var subQ1=sQuery(id+"F0.wireOp",EDGE,"E2");var subQ2=makeQuery(id+"F0.imprint","INTERSECT",VERTEX,{"derivedFrom":[subQ1,subQ0]});Q9=makeQuery(id+"F0.imprint","IMPRINT",FACE,{"disambiguationData":[TD([[makeQuery(id+"F0.imprint","IMPRINT",EDGE,{"disambiguationData":[TD([[subQ2,-1.0]])],"derivedFrom":subQ1}),1.0]])]});}
            var Q10;
            {var subQ0=sQuery(id+"F0.wireOp",EDGE,"E30");var subQ1=sQuery(id+"F0.wireOp",EDGE,"E14");var subQ2=makeQuery(id+"F0.imprint","INTERSECT",VERTEX,{"derivedFrom":[subQ1,subQ0]});Q10=makeQuery(id+"F0.imprint","IMPRINT",FACE,{"disambiguationData":[TD([[makeQuery(id+"F0.imprint","IMPRINT",EDGE,{"disambiguationData":[TD([[subQ2,-1.0]])],"derivedFrom":subQ1}),1.0]])]});}
            extrude(context, id + "F3", {"entities" : qUnion([Q0, Q1, Q2, Q3, Q4, Q5, Q6, Q7, Q8, Q9, Q10]), "operationType" : NewBodyOperationType.ADD, "depth" : .1 * mm});
        }
    });
